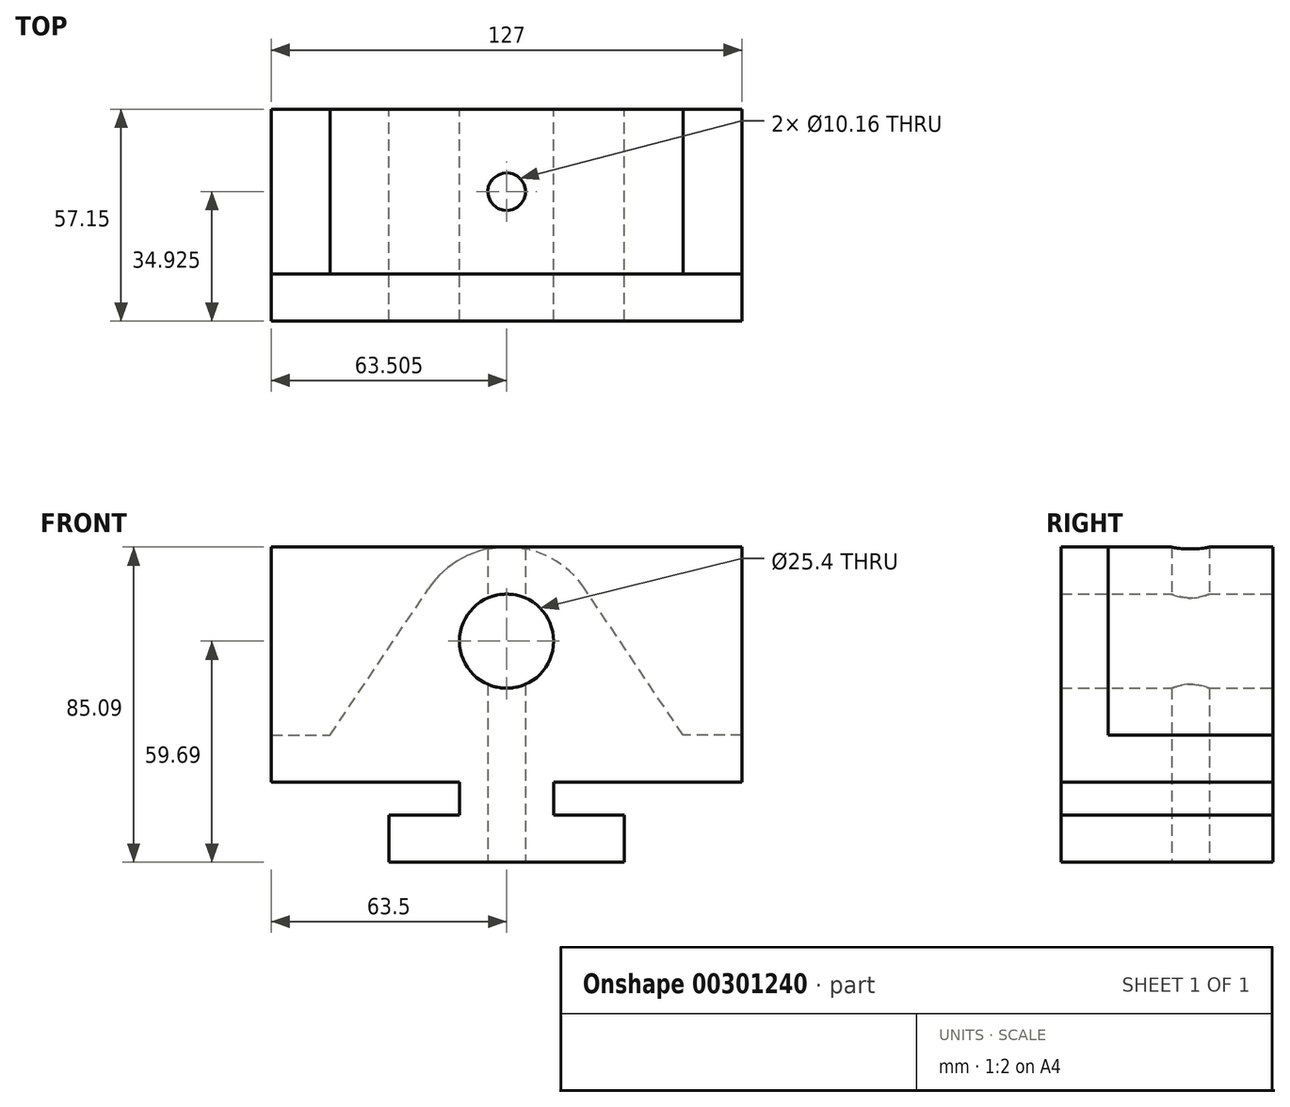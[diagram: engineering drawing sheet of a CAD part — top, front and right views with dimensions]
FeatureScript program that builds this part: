
annotation { "Feature Type Name" : "Feature", "Feature Type Description" : "" }
export const myFeature = defineFeature(function(context is Context, id is Id, definition is map)
    precondition{}
    {
        {
            var Q0;
            Q0=qCreatedBy(makeId("Front.planeOp"),FACE);
            var sketch = newSketch(context, id + "F0", { "sketchPlane" : qUnion([Q0])});
            skLineSegment(sketch, "E0.top", {"start": v(0, 63.5) * mm, "end": v(127, 63.5) * mm});
            skLineSegment(sketch, "E0.left", {"start": v(0, 0) * mm, "end": v(0, 63.5) * mm});
            skLineSegment(sketch, "E0.right", {"start": v(127, 0) * mm, "end": v(127, 63.5) * mm});
            skLineSegment(sketch, "E1", {"start": v(0, 0) * mm, "end": v(0, 12.7) * mm});
            skLineSegment(sketch, "E2", {"start": v(0, 12.7) * mm, "end": v(15.88, 12.7) * mm});
            skLineSegment(sketch, "E3", {"start": v(15.88, 12.7) * mm, "end": v(42.4, 52.25) * mm});
            skLineSegment(sketch, "E4", {"start": v(127, 12.7) * mm, "end": v(111.13, 12.7) * mm});
            skLineSegment(sketch, "E5", {"start": v(111.13, 12.7) * mm, "end": v(84.6, 52.25) * mm});
            skArc(sketch, "E6", {"start": v(42.4, 52.25) * mm, "mid": v(63.5, 63.5) * mm, "end": v(84.6, 52.25) * mm});
            skLineSegment(sketch, "E7", {"start": v(127, 12.7) * mm, "end": v(127, 0) * mm});
            skCircle(sketch, "E8", {"center": v(63.5, 38.1) * mm, "radius": 12.7 * mm});
            skLineSegment(sketch, "E9", {"start": v(0, 0) * mm, "end": v(50.8, 0) * mm});
            skLineSegment(sketch, "E10", {"start": v(127, 0) * mm, "end": v(76.2, 0) * mm});
            skLineSegment(sketch, "E11", {"start": v(50.8, 0) * mm, "end": v(50.8, -8.9) * mm});
            skLineSegment(sketch, "E12", {"start": v(50.8, -8.9) * mm, "end": v(31.75, -8.9) * mm});
            skLineSegment(sketch, "E13", {"start": v(31.75, -8.9) * mm, "end": v(31.75, -21.59) * mm});
            skLineSegment(sketch, "E14", {"start": v(31.75, -21.59) * mm, "end": v(95.25, -21.59) * mm});
            skLineSegment(sketch, "E15", {"start": v(95.25, -21.59) * mm, "end": v(95.25, -8.9) * mm});
            skLineSegment(sketch, "E16", {"start": v(95.25, -8.9) * mm, "end": v(76.2, -8.9) * mm});
            skLineSegment(sketch, "E17", {"start": v(76.2, -8.9) * mm, "end": v(76.2, 0) * mm});
            skSolve(sketch);
        }
        {
            var Q0;
            Q0=makeQuery(id+"F0.imprint","IMPRINT",FACE,{"disambiguationData":[TD([[makeQuery(id+"F0.imprint","IMPRINT",EDGE,{"derivedFrom":sQuery(id+"F0.wireOp",EDGE,"E2")}),-1.0]])]});
            var Q1;
            {var subQ1=sQuery(id+"F0.wireOp",EDGE,"E0.right");Q1=makeQuery(id+"F0.imprint","IMPRINT",FACE,{"disambiguationData":[TD([[makeQuery(id+"F0.imprint","IMPRINT",EDGE,{"derivedFrom":subQ1}),1.0]])]});}
            var Q2;
            {var subQ0=sQuery(id+"F0.wireOp",EDGE,"E0.left");Q2=makeQuery(id+"F0.imprint","IMPRINT",FACE,{"disambiguationData":[TD([[makeQuery(id+"F0.imprint","IMPRINT",EDGE,{"derivedFrom":subQ0}),-1.0]])]});}
            extrude(context, id + "F1", {"entities" : qUnion([Q0, Q1, Q2]), "depth" : 57.15 * mm});
        }
        {
            var Q0;
            {var subQ0=sQuery(id+"F0.wireOp",EDGE,"E0.left");Q0=makeQuery(id+"F0.imprint","IMPRINT",FACE,{"disambiguationData":[TD([[makeQuery(id+"F0.imprint","IMPRINT",EDGE,{"derivedFrom":subQ0}),-1.0]])]});}
            var Q1;
            {var subQ1=sQuery(id+"F0.wireOp",EDGE,"E0.right");Q1=makeQuery(id+"F0.imprint","IMPRINT",FACE,{"disambiguationData":[TD([[makeQuery(id+"F0.imprint","IMPRINT",EDGE,{"derivedFrom":subQ1}),1.0]])]});}
            extrude(context, id + "F2", {"entities" : qUnion([Q0, Q1]), "operationType" : NewBodyOperationType.REMOVE, "depth" : 44.45 * mm});
        }
        {
            var Q0;
            Q0=qCreatedBy(makeId("Top.planeOp"),FACE);
            var sketch = newSketch(context, id + "F3", { "sketchPlane" : qUnion([Q0])});
            skCircle(sketch, "E18", {"center": v(63.5, -22.23) * mm, "radius": 5.08 * mm});
            skSolve(sketch);
        }
        {
            var Q0;
            Q0 = qSketchRegion(id + "F3", true);
            extrude(context, id + "F4", {"entities" : qUnion([Q0]), "operationType" : NewBodyOperationType.REMOVE, "endBound" : BoundingType.THROUGH_ALL, "depth" : 25.4 * mm, "hasSecondDirection" : true, "secondDirectionOppositeDirection" : true, "secondDirectionDepth" : 25.4 * mm});
        }
    });
